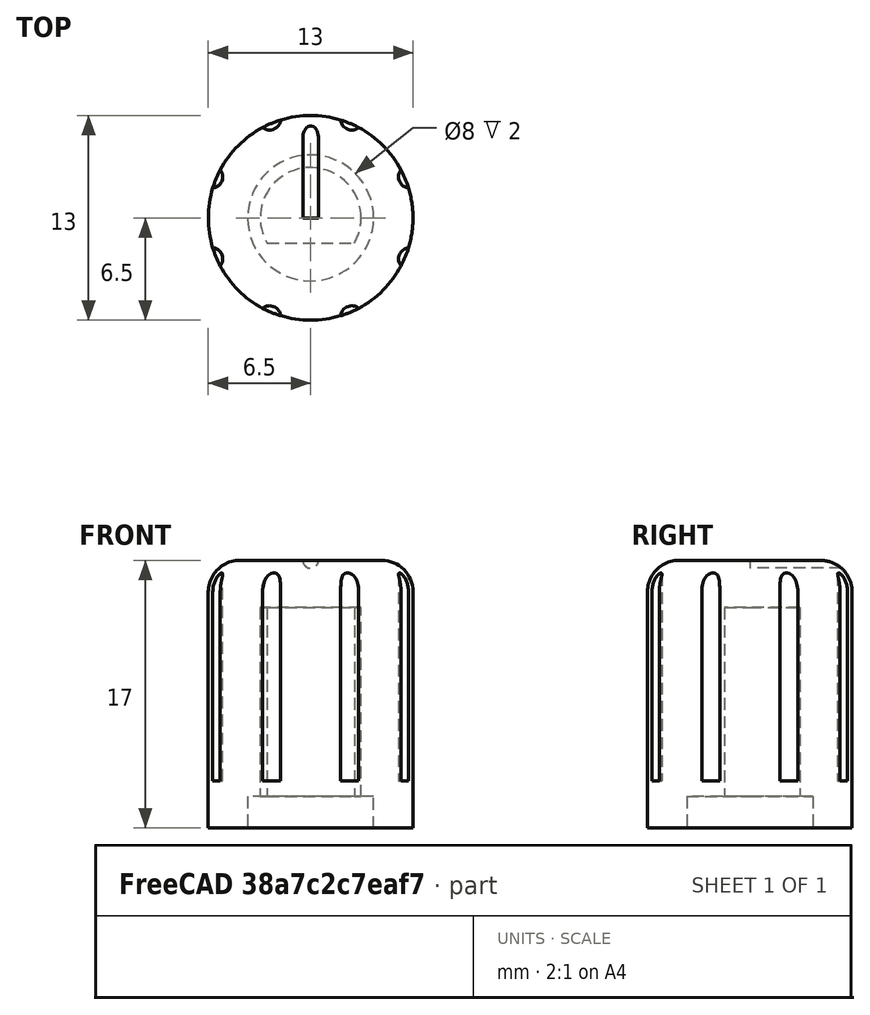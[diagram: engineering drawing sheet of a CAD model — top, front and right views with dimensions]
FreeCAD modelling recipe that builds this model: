
FCSTD DOCUMENT  (FreeCAD 2023.131R26244 +5365 (Git))
Label: knob2
License: All rights reserved
LicenseURL: http://en.wikipedia.org/wiki/All_rights_reserved
objects: Part::Cylinder×14, Part::Cut×4, Part::MultiFuse×3, Part::Box×2, Part::Part2DObjectPython×1, Part::FeaturePython×1, Part::Revolution×1
note: 26 computed .brp shape members not serialized (recipe doc carries the construction recipe); baked Part::Feature solids carry a one-line shape summary decoded from their .brp

FEATURE [Part::Cylinder] cylinder
  Angle = 360
  AttacherType = Attacher::AttachEngine3D
  FirstAngle = 0
  FixShape = 1
  Height = 15
  InvalidShape = false
  Radius = 6.5
  SecondAngle = 0
  TreeRank = 5
  ValidateShape = false
FEATURE [Part::Cylinder] cylinder001
  Angle = 360
  AttacherType = Attacher::AttachEngine3D
  FirstAngle = 0
  FixShape = 1
  Height = 2
  InvalidShape = false
  Placement = pos=(0,0,15) rot=(0,0,1;0rad)
  Radius = 4.5
  SecondAngle = 0
  TreeRank = 6
  ValidateShape = false
FEATURE [Part::Part2DObjectPython] circle  # Draft 2D object (typed FeaturePython)
  Area = 12.5664
  FirstAngle = 0
  FixShape = 1
  InvalidShape = false
  LastAngle = 0
  MakeFace = true
  Placement = pos=(4.5,0,0) rot=(0,0,1;0rad)
  Radius = 2
  TreeRank = 7
  ValidateShape = false
FEATURE [Part::FeaturePython] RefineRotateExtrude  # WARN: FeaturePython — macro-defined, semantics opaque (R4)
  Base = -> circle
  FixShape = 1
  InvalidShape = false
  TreeRank = 8
  ValidateShape = false
FEATURE [Part::Revolution] RotateExtrude
  Angle = 360
  Axis = (0,1,0)
  Base = (0,0,0)
  FaceMakerClass = Part::FaceMakerBullseye
  FixShape = 1
  InvalidShape = false
  Placement = pos=(0,0,15) rot=(1,0,0;1.5708rad)
  Solid = false
  Source = -> RefineRotateExtrude
  Symmetric = false
  TreeRank = 9
  ValidateShape = false
FEATURE [Part::MultiFuse] union
  FixShape = 1
  InvalidShape = false
  Shapes = -> [cylinder,cylinder001,RotateExtrude]
  TreeRank = 10
  ValidateShape = false
FEATURE [Part::Cylinder] cylinder002
  Angle = 360
  AttacherType = Attacher::AttachEngine3D
  FirstAngle = 0
  FixShape = 1
  Height = 6.5
  InvalidShape = false
  Placement = pos=(0,0,17) rot=(-1,0,0;1.5708rad)
  Radius = 0.5
  SecondAngle = 0
  TreeRank = 22
  ValidateShape = false
FEATURE [Part::Cylinder] cylinder003
  Angle = 360
  AttacherType = Attacher::AttachEngine3D
  FirstAngle = 0
  FixShape = 1
  Height = 15
  InvalidShape = false
  Placement = pos=(2.60225,6.28238,3) rot=(0,0,1;0rad)
  Radius = 0.7
  SecondAngle = 0
  TreeRank = 24
  ValidateShape = false
FEATURE [Part::Cylinder] cylinder004
  Angle = 360
  AttacherType = Attacher::AttachEngine3D
  FirstAngle = 0
  FixShape = 1
  Height = 15
  InvalidShape = false
  Placement = pos=(6.28238,2.60225,3) rot=(0,0,1;0rad)
  Radius = 0.7
  SecondAngle = 0
  TreeRank = 25
  ValidateShape = false
FEATURE [Part::Cylinder] cylinder005
  Angle = 360
  AttacherType = Attacher::AttachEngine3D
  FirstAngle = 0
  FixShape = 1
  Height = 15
  InvalidShape = false
  Placement = pos=(6.28238,-2.60225,3) rot=(0,0,1;0rad)
  Radius = 0.7
  SecondAngle = 0
  TreeRank = 26
  ValidateShape = false
FEATURE [Part::Cylinder] cylinder006
  Angle = 360
  AttacherType = Attacher::AttachEngine3D
  FirstAngle = 0
  FixShape = 1
  Height = 15
  InvalidShape = false
  Placement = pos=(2.60225,-6.28238,3) rot=(0,0,1;0rad)
  Radius = 0.7
  SecondAngle = 0
  TreeRank = 27
  ValidateShape = false
FEATURE [Part::Cylinder] cylinder007
  Angle = 360
  AttacherType = Attacher::AttachEngine3D
  FirstAngle = 0
  FixShape = 1
  Height = 15
  InvalidShape = false
  Placement = pos=(-2.60225,-6.28238,3) rot=(0,0,1;0rad)
  Radius = 0.7
  SecondAngle = 0
  TreeRank = 28
  ValidateShape = false
FEATURE [Part::Cylinder] cylinder008
  Angle = 360
  AttacherType = Attacher::AttachEngine3D
  FirstAngle = 0
  FixShape = 1
  Height = 15
  InvalidShape = false
  Placement = pos=(-6.28238,-2.60225,3) rot=(0,0,1;0rad)
  Radius = 0.7
  SecondAngle = 0
  TreeRank = 29
  ValidateShape = false
FEATURE [Part::Cylinder] cylinder009
  Angle = 360
  AttacherType = Attacher::AttachEngine3D
  FirstAngle = 0
  FixShape = 1
  Height = 15
  InvalidShape = false
  Placement = pos=(-6.28238,2.60225,3) rot=(0,0,1;0rad)
  Radius = 0.7
  SecondAngle = 0
  TreeRank = 30
  ValidateShape = false
FEATURE [Part::Cylinder] cylinder010
  Angle = 360
  AttacherType = Attacher::AttachEngine3D
  FirstAngle = 0
  FixShape = 1
  Height = 15
  InvalidShape = false
  Placement = pos=(-2.60225,6.28238,3) rot=(0,0,1;0rad)
  Radius = 0.7
  SecondAngle = 0
  TreeRank = 31
  ValidateShape = false
FEATURE [Part::MultiFuse] Group
  FixShape = 1
  InvalidShape = false
  Shapes = -> [cylinder003,cylinder004,cylinder005,cylinder006,cylinder007,cylinder008,cylinder009,cylinder010]
  TreeRank = 32
  ValidateShape = false
FEATURE [Part::Cylinder] cylinder011
  Angle = 360
  AttacherType = Attacher::AttachEngine3D
  FirstAngle = 0
  FixShape = 1
  Height = 12
  InvalidShape = false
  Placement = pos=(0,0,2) rot=(0,0,1;0rad)
  Radius = 3.2
  SecondAngle = 0
  TreeRank = 36
  ValidateShape = false
FEATURE [Part::Box] cube
  AttacherType = Attacher::AttachEngine3D
  FixShape = 1
  Height = 12
  InvalidShape = false
  Length = 10
  Placement = pos=(-5,-6.6,2) rot=(0,0,1;0rad)
  TreeRank = 37
  ValidateShape = false
  Width = 5
FEATURE [Part::Cut] difference
  Base = -> cylinder011
  FixShape = 1
  InvalidShape = false
  Tool = -> cube
  TreeRank = 38
  ValidateShape = false
FEATURE [Part::Cylinder] cylinder012
  Angle = 360
  AttacherType = Attacher::AttachEngine3D
  FirstAngle = 0
  FixShape = 1
  Height = 2
  InvalidShape = false
  Radius = 3.2
  SecondAngle = 0
  TreeRank = 42
  ValidateShape = false
FEATURE [Part::Box] cube001
  AttacherType = Attacher::AttachEngine3D
  FixShape = 1
  Height = 8
  InvalidShape = false
  Length = 10
  Placement = pos=(-5,-6.6,0) rot=(0,0,1;0rad)
  TreeRank = 43
  ValidateShape = false
  Width = 5
FEATURE [Part::Cut] difference001
  Base = -> cylinder012
  FixShape = 1
  InvalidShape = false
  Tool = -> cube001
  TreeRank = 44
  ValidateShape = false
FEATURE [Part::MultiFuse] union001
  FixShape = 1
  InvalidShape = false
  Shapes = -> [cylinder002,Group,difference,difference001]
  TreeRank = 46
  ValidateShape = false
FEATURE [Part::Cut] difference002
  Base = -> union
  FixShape = 1
  InvalidShape = false
  Tool = -> union001
  TreeRank = 45
  ValidateShape = false
FEATURE [Part::Cylinder] Cylinder
  Angle = 360
  AttacherType = Attacher::AttachEngine3D
  FirstAngle = 0
  FixShape = 1
  Height = 2
  InvalidShape = false
  Radius = 4
  SecondAngle = 0
  TreeRank = 47
  ValidateShape = false
FEATURE [Part::Cut] Cut
  Base = -> difference002
  FixShape = 1
  InvalidShape = false
  Tool = -> Cylinder
  TreeRank = 48
  ValidateShape = false
